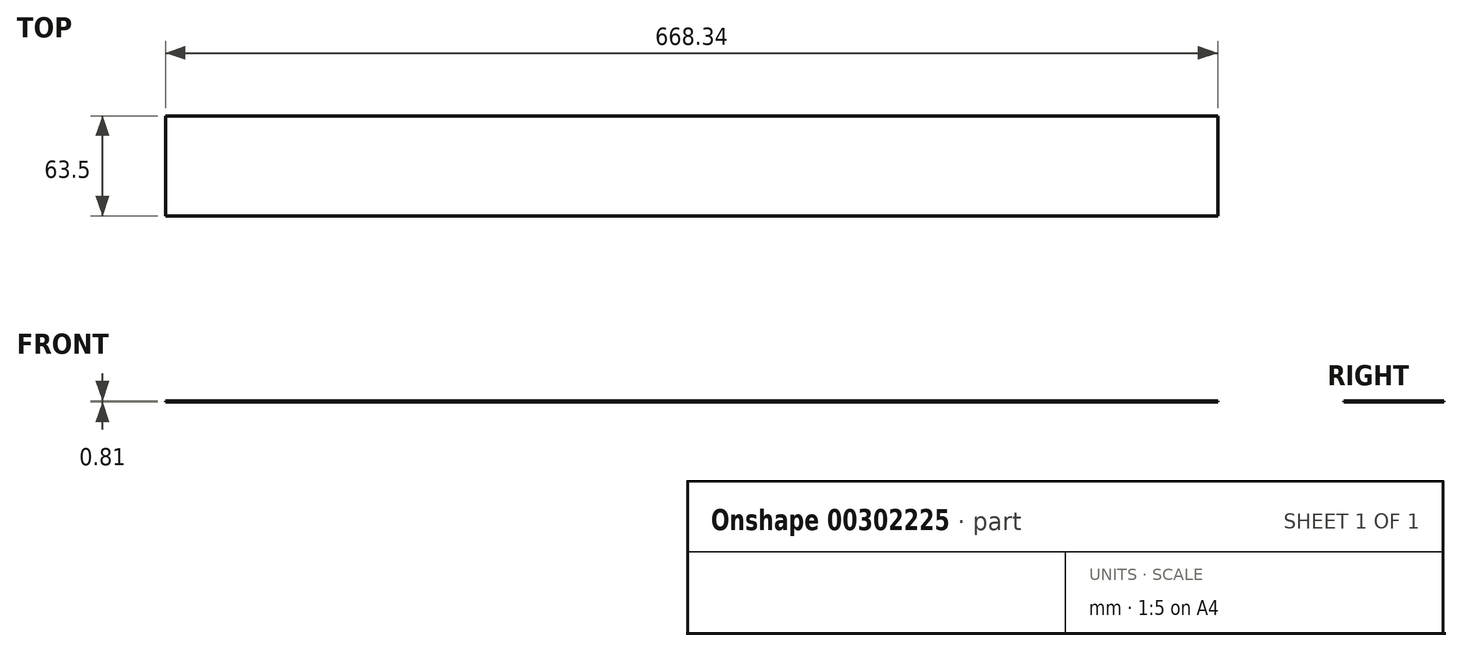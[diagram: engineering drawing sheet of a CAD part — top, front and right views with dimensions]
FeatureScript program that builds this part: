
annotation { "Feature Type Name" : "Feature", "Feature Type Description" : "" }
export const myFeature = defineFeature(function(context is Context, id is Id, definition is map)
    precondition{}
    {
        {
            var Q0;
            Q0=qCreatedBy(makeId("Top.planeOp"),FACE);
            var sketch = newSketch(context, id + "F0", { "sketchPlane" : qUnion([Q0])});
            skLineSegment(sketch, "E0.bottom", {"start": v(0, 0) * mm, "end": v(668.34, 0) * mm});
            skLineSegment(sketch, "E0.top", {"start": v(0, 63.5) * mm, "end": v(668.34, 63.5) * mm});
            skLineSegment(sketch, "E0.left", {"start": v(0, 0) * mm, "end": v(0, 63.5) * mm});
            skLineSegment(sketch, "E0.right", {"start": v(668.34, 0) * mm, "end": v(668.34, 63.5) * mm});
            skLineSegment(sketch, "E1.bottom", {"start": v(655.64, 0) * mm, "end": v(623.89, 0) * mm});
            skLineSegment(sketch, "E1.top", {"start": v(655.64, -69.85) * mm, "end": v(623.89, -69.85) * mm});
            skLineSegment(sketch, "E1.left", {"start": v(655.64, 0) * mm, "end": v(655.64, -69.85) * mm});
            skLineSegment(sketch, "E1.right", {"start": v(623.89, 0) * mm, "end": v(623.89, -69.85) * mm});
            skLineSegment(sketch, "E2.bottom", {"start": v(563.56, 0) * mm, "end": v(241.85, 0) * mm});
            skLineSegment(sketch, "E2.top", {"start": v(563.56, -69.85) * mm, "end": v(241.85, -69.85) * mm});
            skLineSegment(sketch, "E2.left", {"start": v(563.56, 0) * mm, "end": v(563.56, -69.85) * mm});
            skLineSegment(sketch, "E2.right", {"start": v(241.85, 0) * mm, "end": v(241.85, -69.85) * mm});
            skLineSegment(sketch, "E3.bottom", {"start": v(133.9, 0) * mm, "end": v(83.1, 0) * mm});
            skLineSegment(sketch, "E3.top", {"start": v(133.9, -69.85) * mm, "end": v(83.1, -69.85) * mm});
            skLineSegment(sketch, "E3.left", {"start": v(133.9, 0) * mm, "end": v(133.9, -69.85) * mm});
            skLineSegment(sketch, "E3.right", {"start": v(83.1, 0) * mm, "end": v(83.1, -69.85) * mm});
            skSolve(sketch);
        }
        {
            var Q0;
            Q0=makeQuery(id+"F0.imprint","IMPRINT",FACE,{"disambiguationData":[TD([[makeQuery(id+"F0.imprint","IMPRINT",EDGE,{"derivedFrom":sQuery(id+"F0.wireOp",EDGE,"E0.top")}),-1.0]])]});
            var Q1;
            Q1=makeQuery(id+"F0.imprint","IMPRINT",FACE,{"disambiguationData":[TD([[makeQuery(id+"F0.imprint","IMPRINT",EDGE,{"derivedFrom":sQuery(id+"F0.wireOp",EDGE,"E3.bottom")}),1.0]])]});
            var Q2;
            Q2=makeQuery(id+"F0.imprint","IMPRINT",FACE,{"disambiguationData":[TD([[makeQuery(id+"F0.imprint","IMPRINT",EDGE,{"derivedFrom":sQuery(id+"F0.wireOp",EDGE,"E2.bottom")}),1.0]])]});
            var Q3;
            Q3=makeQuery(id+"F0.imprint","IMPRINT",FACE,{"disambiguationData":[TD([[makeQuery(id+"F0.imprint","IMPRINT",EDGE,{"derivedFrom":sQuery(id+"F0.wireOp",EDGE,"E1.bottom")}),1.0]])]});
            extrude(context, id + "F1", {"entities" : qUnion([Q0, Q1, Q2, Q3]), "depth" : 0.81 * mm});
        }
    });
